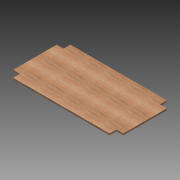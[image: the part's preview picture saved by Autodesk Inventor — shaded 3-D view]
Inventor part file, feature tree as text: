
AUTODESK INVENTOR PART (.ipt)
format: ipt  version: 2013 (Build 170138000, 138)  size: 104,448 bytes
history: native  units: in
note: dims shown in document units (in); Inventor stores cm internally (conversion verified against a paired STEP export)
features: extrude x1, sketch x1
ambient origin geometry x8: Origin, YZ Plane, XZ Plane, XY Plane, X Axis, Y Axis, Z Axis, Center Point
bodies: Solid1 (feature_tree)
feature tree (2):
  extrude  "Extrusion1"  Depth=3.25in
  sketch  "Sketch1"  dims[d2=3.25in d3=3.25in d4=3.25in d5=3.25in d6=3.25in d7=3.25in d8=3.25in d9=3.25in d10=90.0deg d11=90.0deg d12=90.0deg d13=90.0deg d14=90.0deg d15=90.0deg d16=90.0deg d17=90.0deg d18=0.75in d19=0.0in d20=27.0in]
